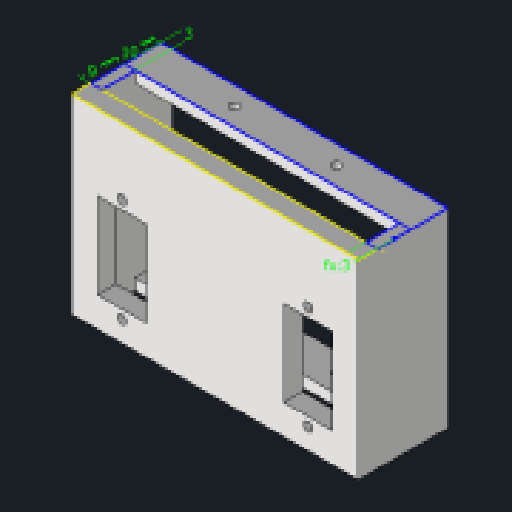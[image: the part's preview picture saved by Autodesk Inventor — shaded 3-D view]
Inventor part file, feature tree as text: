
AUTODESK INVENTOR PART (.ipt)
format: ipt  version: 2023.2 (Build 272271030, 271C)  size: 379,392 bytes
history: native  units: mm
features: sketch x5, extrude x4, projected_geometry x4, hole x2
ambient origin geometry x8: Origin, YZ Plane, XZ Plane, XY Plane, X Axis, Y Axis, Z Axis, Center Point
bodies: Solid1 (feature_tree)
feature tree (15):
  extrude  "Extrusion1"  Depth=5.0mm TaperAngle=0.0deg
  hole  "Hole1"  [1 undecoded]
  sketch  "Sketch4"  dims[d7=7.0mm d8=27.8mm]
  extrude  "Extrusion2"  Depth=7.0mm
  extrude  "Extrusion3"  Depth=2.4mm
  extrude  "Extrusion4"  Depth=50.0mm
  hole  "Hole2"  [1 undecoded]
  sketch  "Sketch1"  dims[d1=51.3mm d2=5.0mm d3=0.0mm]
  sketch  "Sketch3"  dims[d4=23.0mm d5=13.0mm]
  projected_geometry  "Projected Loop1"
  projected_geometry  "Projected Loop2"
  sketch  "Sketch5"  dims[d9=2.4mm d10=2.4mm]
  projected_geometry  "Projected Loop3"
  sketch  "Sketch6"  dims[d11=2.5mm d12=6.0mm d13=4.0mm d14=2.0mm d15=90.0deg d16=15.664mm d17=20.594885mm d18=50.0mm d19=7.0mm d20=8.0mm d21=12.0mm d22=8.0mm d23=20.0mm d24=20.0mm d25=3.0mm d26=0.0mm d27=3.0mm d28=0.0mm d29=5.0mm d30=0.0mm d31=27.25mm d32=27.25mm d33=6.05mm d34=6.5mm d35=6.0mm d36=4.0mm d37=2.0mm d38=90.0deg d39=8.0mm d40=20.594885mm d41=5.95mm d42=3.0mm d43=3.0mm]
  projected_geometry  "Projected Loop4"
note: 2 required parameter values undecoded (feature->parameter linkage not recoverable at this tier; creation-order binding heuristic only, values carry confidence <= 0.55)
